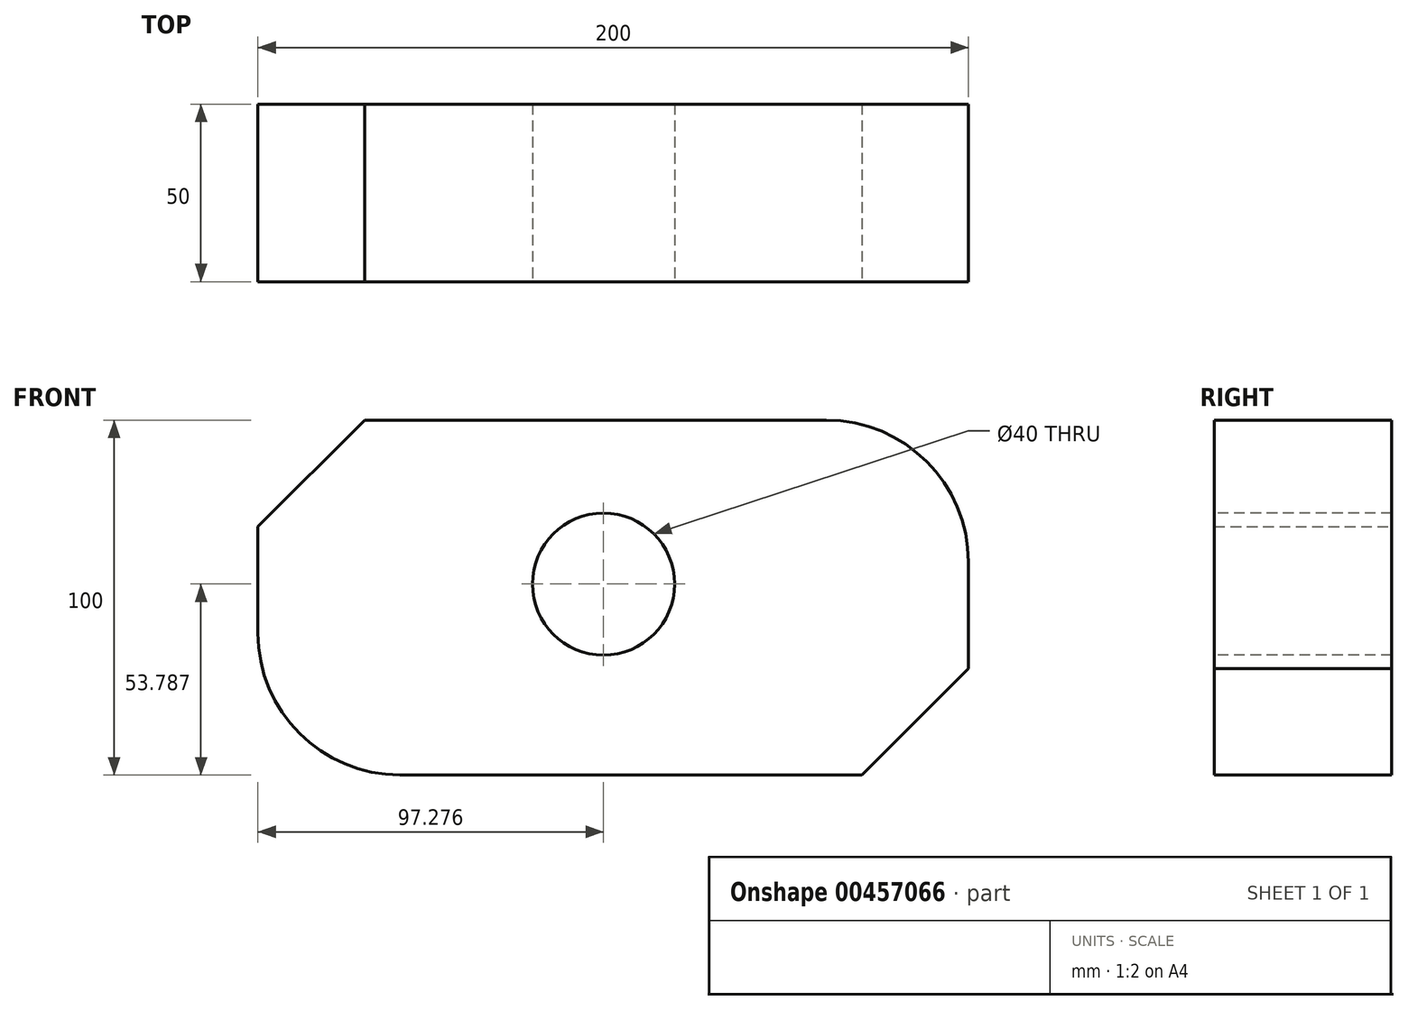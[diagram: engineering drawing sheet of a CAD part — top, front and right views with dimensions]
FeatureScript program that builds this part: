
annotation { "Feature Type Name" : "Feature", "Feature Type Description" : "" }
export const myFeature = defineFeature(function(context is Context, id is Id, definition is map)
    precondition{}
    {
        {
            var Q0;
            Q0=qCreatedBy(makeId("Front.planeOp"),FACE);
            var sketch = newSketch(context, id + "F0", { "sketchPlane" : qUnion([Q0])});
            skLineSegment(sketch, "E0.bottom", {"start": v(0, 0) * mm, "end": v(-200, 0) * mm});
            skLineSegment(sketch, "E0.top", {"start": v(0, 100) * mm, "end": v(-200, 100) * mm});
            skLineSegment(sketch, "E0.left", {"start": v(0, 0) * mm, "end": v(0, 100) * mm});
            skLineSegment(sketch, "E0.right", {"start": v(-200, 0) * mm, "end": v(-200, 100) * mm});
            skSolve(sketch);
        }
        {
            var Q0;
            Q0=makeQuery(id+"F0.imprint","IMPRINT",FACE,{"disambiguationData":[TD([[makeQuery(id+"F0.imprint","IMPRINT",EDGE,{"derivedFrom":sQuery(id+"F0.wireOp",EDGE,"E0.bottom")}),-1.0]])]});
            extrude(context, id + "F1", {"entities" : qUnion([Q0]), "depth" : 50 * mm});
        }
        {
            var Q0;
            Q0=makeQuery(id+"F1.opExtrude","SWEPT_EDGE",EDGE,{"disambiguationData":[OSD([sQuery(id+"F0.wireOp",EDGE,"E0.top"),sQuery(id+"F0.wireOp",EDGE,"E0.right")])]});
            chamfer(context, id + "F2", {"entities" : qUnion([Q0]), "width" : 30 * mm, "tangentPropagation" : true});
        }
        {
            var Q0;
            Q0=makeQuery(id+"F1.opExtrude","SWEPT_EDGE",EDGE,{"disambiguationData":[OSD([sQuery(id+"F0.wireOp",EDGE,"E0.bottom"),sQuery(id+"F0.wireOp",EDGE,"E0.left")])]});
            chamfer(context, id + "F3", {"entities" : qUnion([Q0]), "width" : 30 * mm, "tangentPropagation" : true});
        }
        {
            var Q0;
            Q0=makeQuery(id+"F1.opExtrude","SWEPT_EDGE",EDGE,{"disambiguationData":[OSD([sQuery(id+"F0.wireOp",EDGE,"E0.top"),sQuery(id+"F0.wireOp",EDGE,"E0.left")])]});
            fillet(context, id + "F4", {"entities" : qUnion([Q0]), "radius" : 40 * mm, "tangentPropagation" : true, "allowEdgeOverflow" : false});
        }
        {
            var Q0;
            Q0=makeQuery(id+"F1.opExtrude","SWEPT_EDGE",EDGE,{"disambiguationData":[OSD([sQuery(id+"F0.wireOp",EDGE,"E0.bottom"),sQuery(id+"F0.wireOp",EDGE,"E0.right")])]});
            fillet(context, id + "F5", {"entities" : qUnion([Q0]), "radius" : 40 * mm, "tangentPropagation" : true, "allowEdgeOverflow" : false});
        }
        {
            var Q0;
            Q0=makeQuery(id+"F1.opExtrude","CAP_FACE",FACE,{"disambiguationData":[OSD([sQuery(id+"F0.wireOp",EDGE,"E0.bottom"),sQuery(id+"F0.wireOp",EDGE,"E0.top"),sQuery(id+"F0.wireOp",EDGE,"E0.left"),sQuery(id+"F0.wireOp",EDGE,"E0.right")])],"isStart":false});
            var sketch = newSketch(context, id + "F6", { "sketchPlane" : qUnion([Q0])});
            skCircle(sketch, "E1", {"center": v(-102.72, 53.79) * mm, "radius": 20 * mm});
            skSolve(sketch);
        }
        {
            var Q0;
            Q0=sQuery(id+"F6.wireOp",VERTEX,"E1.center");
            var Q1;
            Q1=makeQuery(id+"F1.opExtrude","SWEPT_BODY",BODY,{"disambiguationData":[OSD([sQuery(id+"F0.wireOp",EDGE,"E0.bottom"),sQuery(id+"F0.wireOp",EDGE,"E0.top"),sQuery(id+"F0.wireOp",EDGE,"E0.left"),sQuery(id+"F0.wireOp",EDGE,"E0.right")])]});
            hole(context, id + "F7", {"style" : HoleStyle.SIMPLE, "endStyle" : HoleEndStyle.THROUGH, "holeDiameter" : 40 * mm, "isTappedThrough" : true, "tappedDepth" : 12 * mm, "tapClearance" : 3, "startFromSketch" : true, "locations" : qUnion([Q0]), "scope" : qUnion([Q1])});
        }
    });
